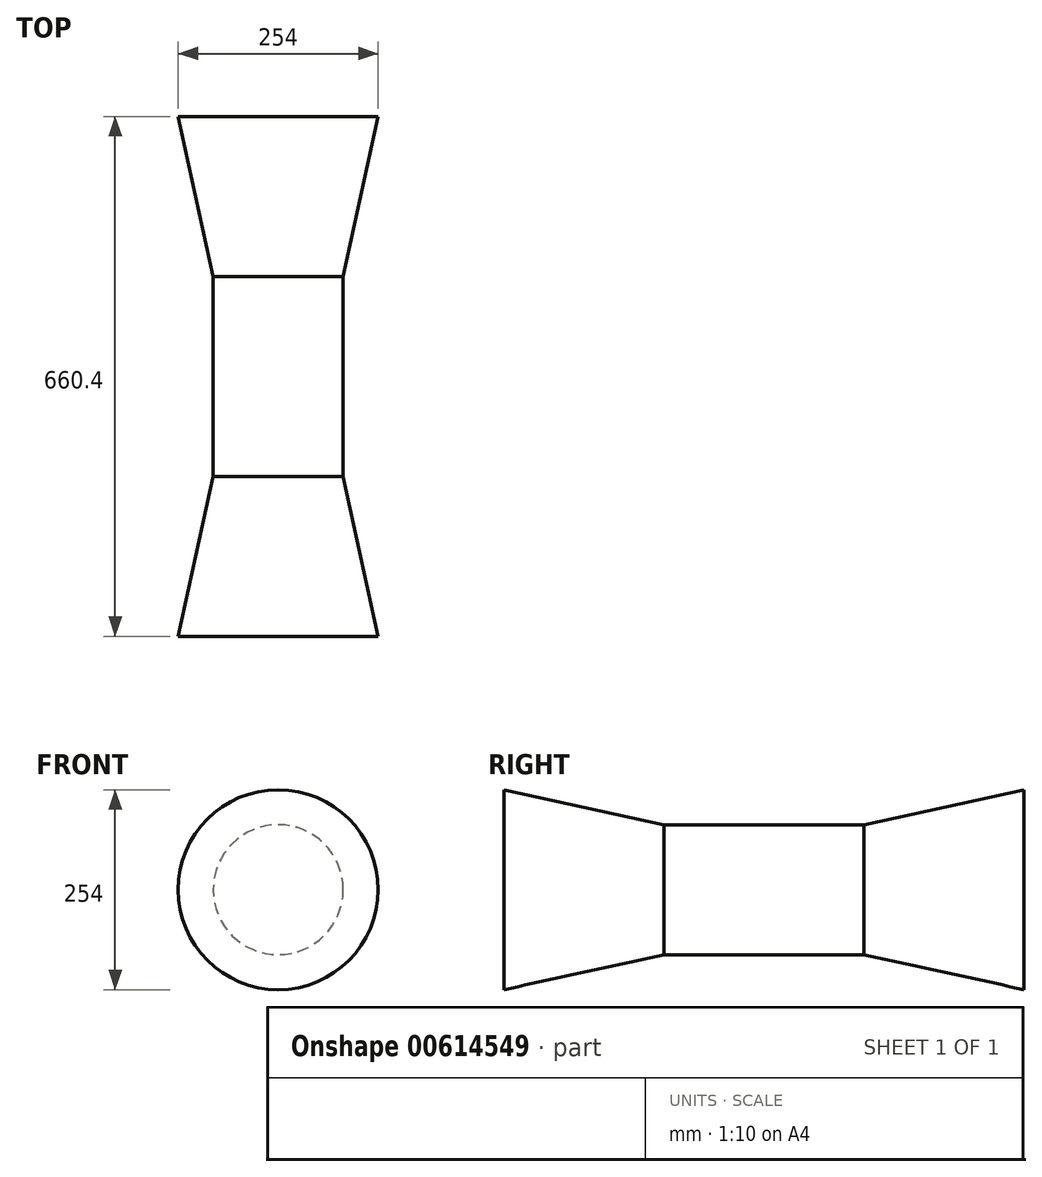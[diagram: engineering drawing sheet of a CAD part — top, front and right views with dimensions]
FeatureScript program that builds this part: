
annotation { "Feature Type Name" : "Feature", "Feature Type Description" : "" }
export const myFeature = defineFeature(function(context is Context, id is Id, definition is map)
    precondition{}
    {
        {
            var Q0;
            Q0=qCreatedBy(makeId("Front.planeOp"),FACE);
            var sketch = newSketch(context, id + "F0", { "sketchPlane" : qUnion([Q0])});
            skCircle(sketch, "E0", {"center": v(0, 0) * mm, "radius": 127 * mm});
            skSolve(sketch);
        }
        {
            var Q0;
            Q0=qCreatedBy(makeId("Front.planeOp"),FACE);
            cPlane(context, id + "F1", {"entities" : qUnion([Q0]), "cplaneType" : CPlaneType.OFFSET, "offset" : 203.2 * mm, "oppositeDirection" : true, "width" : 152.4 * mm, "height" : 152.4 * mm});
        }
        {
            var Q0;
            Q0=qCreatedBy(id+"F1.planeOp",FACE);
            var sketch = newSketch(context, id + "F2", { "sketchPlane" : qUnion([Q0])});
            skCircle(sketch, "E1", {"center": v(0, 0) * mm, "radius": 82.55 * mm});
            skSolve(sketch);
        }
        {
            var Q0;
            Q0=makeQuery(id+"F0.imprint","IMPRINT",FACE,{"disambiguationData":[TD([[makeQuery(id+"F0.imprint","IMPRINT",EDGE,{"derivedFrom":sQuery(id+"F0.wireOp",EDGE,"E0")}),1.0]])]});
            var Q1;
            Q1=makeQuery(id+"F2.imprint","IMPRINT",FACE,{"disambiguationData":[TD([[makeQuery(id+"F2.imprint","IMPRINT",EDGE,{"derivedFrom":sQuery(id+"F2.wireOp",EDGE,"E1")}),1.0]])]});
            loft(context, id + "F3", {"sheetProfilesArray" : [{ "sheetProfileEntities" : qUnion([Q0]) }, { "sheetProfileEntities" : qUnion([Q1]) }]});
        }
        {
            var Q0;
            Q0=qCreatedBy(id+"F1.planeOp",FACE);
            var sketch = newSketch(context, id + "F4", { "sketchPlane" : qUnion([Q0])});
            skCircle(sketch, "E2", {"center": v(0, 0) * mm, "radius": 82.55 * mm});
            skSolve(sketch);
        }
        {
            var Q0;
            Q0 = qSketchRegion(id + "F4", true);
            extrude(context, id + "F5", {"entities" : qUnion([Q0]), "operationType" : NewBodyOperationType.ADD, "oppositeDirection" : true, "depth" : 254 * mm, "offsetDistance" : 25.4 * mm});
        }
        {
            var Q0;
            Q0=qCreatedBy(id+"F1.planeOp",FACE);
            cPlane(context, id + "F6", {"entities" : qUnion([Q0]), "cplaneType" : CPlaneType.OFFSET, "offset" : 457.2 * mm, "oppositeDirection" : true, "width" : 152.4 * mm, "height" : 152.4 * mm});
        }
        {
            var Q0;
            Q0=qCreatedBy(id+"F6.planeOp",FACE);
            var sketch = newSketch(context, id + "F7", { "sketchPlane" : qUnion([Q0])});
            skCircle(sketch, "E3", {"center": v(0, 0) * mm, "radius": 127 * mm});
            skSolve(sketch);
        }
        {
            var Q1;
            Q1=makeQuery(id+"F5.opExtrude","CAP_FACE",FACE,{"disambiguationData":[OSD([sQuery(id+"F4.wireOp",EDGE,"E2")])],"isStart":false});
            var Q2;
            Q2=makeQuery(id+"F7.imprint","IMPRINT",FACE,{"disambiguationData":[TD([[makeQuery(id+"F7.imprint","IMPRINT",EDGE,{"derivedFrom":sQuery(id+"F7.wireOp",EDGE,"E3")}),1.0]])]});
            loft(context, id + "F8", {"operationType" : NewBodyOperationType.ADD, "sheetProfilesArray" : [{ "sheetProfileEntities" : qUnion([Q1]) }, { "sheetProfileEntities" : qUnion([Q2]) }]});
        }
    });
